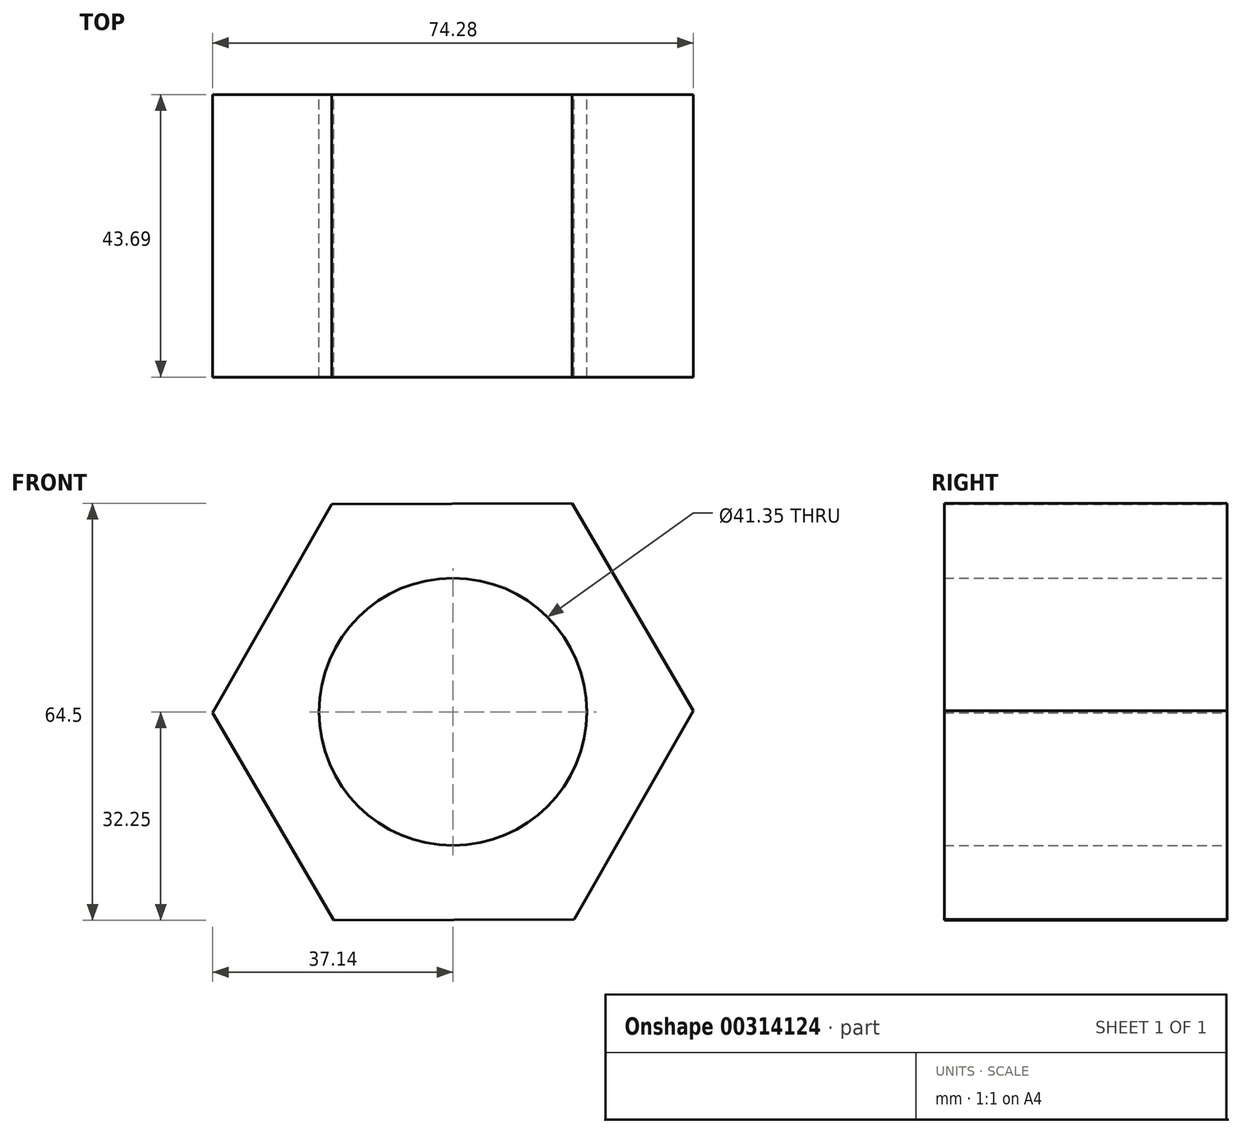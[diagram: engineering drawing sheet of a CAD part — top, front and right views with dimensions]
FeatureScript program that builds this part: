
annotation { "Feature Type Name" : "Feature", "Feature Type Description" : "" }
export const myFeature = defineFeature(function(context is Context, id is Id, definition is map)
    precondition{}
    {
        {
            var Q0;
            Q0=qCreatedBy(makeId("Front.planeOp"),FACE);
            var sketch = newSketch(context, id + "F0", { "sketchPlane" : qUnion([Q0])});
            skCircle(sketch, "E0", {"center": v(0, 0) * mm, "radius": 20.67 * mm});
            skSolve(sketch);
        }
        {
            var Q0;
            Q0=makeQuery(id+"F0.imprint","IMPRINT",FACE,{"disambiguationData":[TD([[makeQuery(id+"F0.imprint","IMPRINT",EDGE,{"derivedFrom":sQuery(id+"F0.wireOp",EDGE,"E0")}),1.0]])]});
            var sketch = newSketch(context, id + "F1", { "sketchPlane" : qUnion([Q0])});
            skCircle(sketch, "E1.cCircle", {"center": v(0, 0) * mm, "radius": 32.17 * mm, "construction": true});
            skLineSegment(sketch, "E1.0", {"start": v(18.43, 32.25) * mm, "end": v(37.14, 0.17) * mm});
            skLineSegment(sketch, "E1.1", {"start": v(37.14, 0.17) * mm, "end": v(18.72, -32.08) * mm});
            skLineSegment(sketch, "E1.2", {"start": v(18.72, -32.08) * mm, "end": v(-18.43, -32.25) * mm});
            skLineSegment(sketch, "E1.3", {"start": v(-18.43, -32.25) * mm, "end": v(-37.14, -0.17) * mm});
            skLineSegment(sketch, "E1.4", {"start": v(-37.14, -0.17) * mm, "end": v(-18.72, 32.08) * mm});
            skLineSegment(sketch, "E1.5", {"start": v(-18.72, 32.08) * mm, "end": v(18.43, 32.25) * mm});
            skPoint(sketch, "E1.0.midPoint", {"position": v(27.78, 16.2) * mm});
            skSolve(sketch);
        }
        {
            var Q0;
            Q0=makeQuery(id+"F1.imprint","IMPRINT",FACE,{"disambiguationData":[TD([[makeQuery(id+"F1.imprint","IMPRINT",EDGE,{"derivedFrom":sQuery(id+"F1.wireOp",EDGE,"E1.0")}),-1.0]])]});
            extrude(context, id + "F2", {"entities" : qUnion([Q0]), "depth" : 43.69 * mm});
        }
    });
